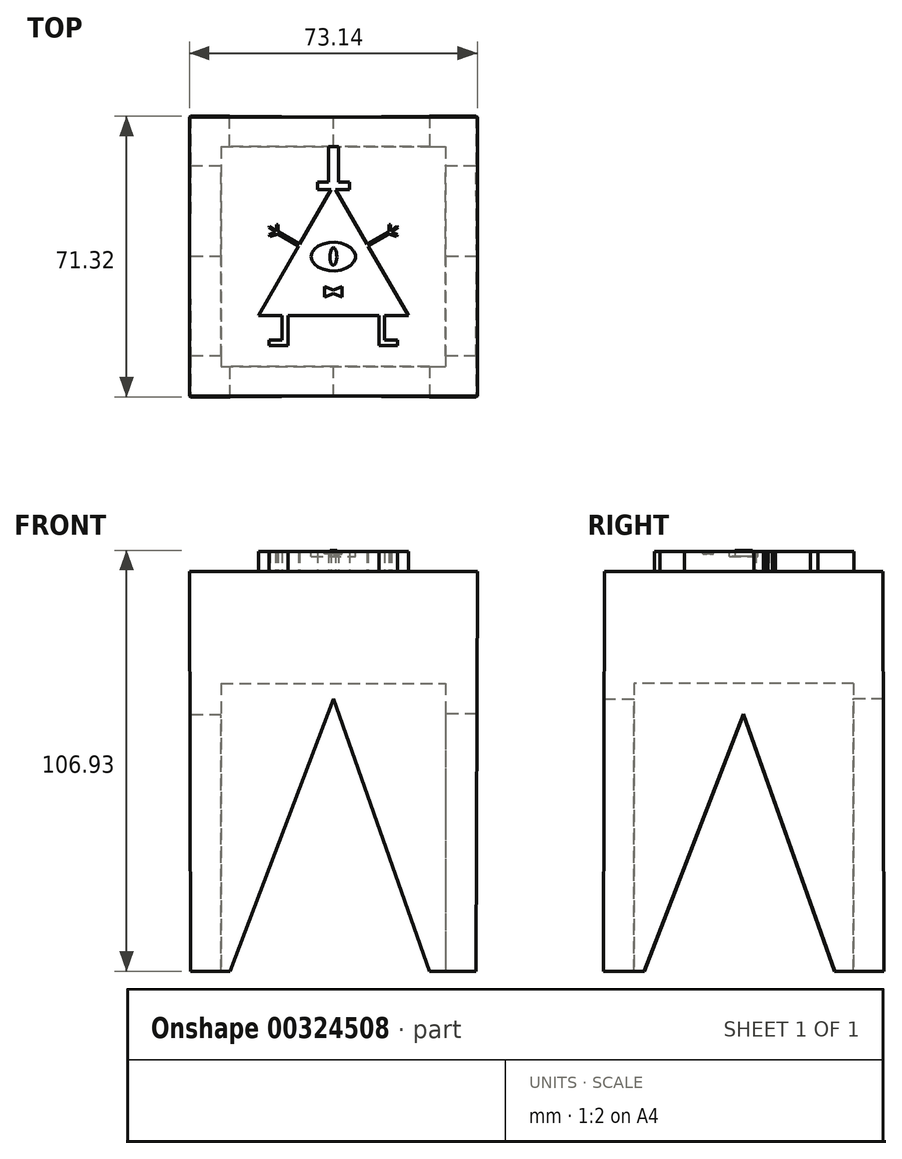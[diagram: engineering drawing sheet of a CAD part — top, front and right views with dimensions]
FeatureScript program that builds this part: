
annotation { "Feature Type Name" : "Feature", "Feature Type Description" : "" }
export const myFeature = defineFeature(function(context is Context, id is Id, definition is map)
    precondition{}
    {
        {
            var Q0;
            Q0=qCreatedBy(makeId("Top.planeOp"),FACE);
            var sketch = newSketch(context, id + "F0", { "sketchPlane" : qUnion([Q0])});
            skLineSegment(sketch, "E0.bottom", {"start": v(-36.23, 35.66) * mm, "end": v(36.23, 35.66) * mm});
            skLineSegment(sketch, "E0.top", {"start": v(-36.23, -35.66) * mm, "end": v(36.23, -35.66) * mm});
            skLineSegment(sketch, "E0.left", {"start": v(-36.23, 35.66) * mm, "end": v(-36.23, -35.66) * mm});
            skLineSegment(sketch, "E0.right", {"start": v(36.23, 35.66) * mm, "end": v(36.23, -35.66) * mm});
            skPoint(sketch, "E0.middle", {"position": v(0, 0) * mm});
            skSolve(sketch);
        }
        {
            var Q0;
            Q0=qCreatedBy(makeId("Top.planeOp"),FACE);
            cPlane(context, id + "F1", {"entities" : qUnion([Q0]), "cplaneType" : CPlaneType.OFFSET, "offset" : 101.6 * mm, "width" : 152.4 * mm, "height" : 152.4 * mm});
        }
        {
            var Q0;
            Q0=qCreatedBy(id+"F1.planeOp",FACE);
            var sketch = newSketch(context, id + "F2", { "sketchPlane" : qUnion([Q0])});
            skLineSegment(sketch, "E1.bottom", {"start": v(-36.57, 35.42) * mm, "end": v(36.57, 35.42) * mm});
            skLineSegment(sketch, "E1.top", {"start": v(-36.57, -35.42) * mm, "end": v(36.57, -35.42) * mm});
            skLineSegment(sketch, "E1.left", {"start": v(-36.57, 35.42) * mm, "end": v(-36.57, -35.42) * mm});
            skLineSegment(sketch, "E1.right", {"start": v(36.57, 35.42) * mm, "end": v(36.57, -35.42) * mm});
            skPoint(sketch, "E1.middle", {"position": v(0, 0) * mm});
            skSolve(sketch);
        }
        {
            var Q0;
            Q0=makeQuery(id+"F2.imprint","IMPRINT",FACE,{"disambiguationData":[TD([[makeQuery(id+"F2.imprint","IMPRINT",EDGE,{"derivedFrom":sQuery(id+"F2.wireOp",EDGE,"E1.bottom")}),-1.0]])]});
            var Q1;
            Q1=makeQuery(id+"F0.imprint","IMPRINT",FACE,{"disambiguationData":[TD([[makeQuery(id+"F0.imprint","IMPRINT",EDGE,{"derivedFrom":sQuery(id+"F0.wireOp",EDGE,"E0.bottom")}),-1.0]])]});
            loft(context, id + "F3", {"sheetProfilesArray" : [{ "sheetProfileEntities" : qUnion([Q0]) }, { "sheetProfileEntities" : qUnion([Q1]) }]});
        }
        {
            var Q0;
            Q0=makeQuery(id+"F3.opLoft","SWEPT_FACE",FACE,{"disambiguationData":[OSD([sQuery(id+"F0.wireOp",EDGE,"E0.bottom"),sQuery(id+"F0.wireOp",EDGE,"E0.top"),sQuery(id+"F0.wireOp",EDGE,"E0.left"),sQuery(id+"F2.wireOp",EDGE,"E1.bottom"),sQuery(id+"F2.wireOp",EDGE,"E1.top"),sQuery(id+"F2.wireOp",EDGE,"E1.left")])]});
            var sketch = newSketch(context, id + "F4", { "sketchPlane" : qUnion([Q0])});
            skLineSegment(sketch, "E2", {"start": v(-24.16, -2.93) * mm, "end": v(0, 65.28) * mm});
            skLineSegment(sketch, "E3", {"start": v(0, 65.28) * mm, "end": v(26.31, -2.66) * mm});
            skLineSegment(sketch, "E4", {"start": v(26.31, -2.66) * mm, "end": v(-24.16, -2.93) * mm});
            skSolve(sketch);
        }
        {
            var Q0;
            Q0=makeQuery(id+"F3.opLoft","CAP_FACE",FACE,{"disambiguationData":[OSD([makeQuery(id+"F0.imprint","IMPRINT",FACE,{"disambiguationData":[TD([[makeQuery(id+"F0.imprint","IMPRINT",EDGE,{"derivedFrom":sQuery(id+"F0.wireOp",EDGE,"E0.bottom")}),-1.0]])]})])],"isStart":true});
            var sketch = newSketch(context, id + "F5", { "sketchPlane" : qUnion([Q0])});
            skLineSegment(sketch, "E5.bottom", {"start": v(-28.48, -27.93) * mm, "end": v(28.48, -27.93) * mm});
            skLineSegment(sketch, "E5.top", {"start": v(-28.48, 27.93) * mm, "end": v(28.48, 27.93) * mm});
            skLineSegment(sketch, "E5.left", {"start": v(-28.48, -27.93) * mm, "end": v(-28.48, 27.93) * mm});
            skLineSegment(sketch, "E5.right", {"start": v(28.48, -27.93) * mm, "end": v(28.48, 27.93) * mm});
            skPoint(sketch, "E5.middle", {"position": v(0, 0) * mm});
            skSolve(sketch);
        }
        {
            var Q0;
            Q0 = qSketchRegion(id + "F5", true);
            extrude(context, id + "F6", {"entities" : qUnion([Q0]), "operationType" : NewBodyOperationType.REMOVE, "oppositeDirection" : true, "depth" : 73.15 * mm});
        }
        {
            var Q0;
            Q0 = qSketchRegion(id + "F4", true);
            extrude(context, id + "F7", {"entities" : qUnion([Q0]), "operationType" : NewBodyOperationType.REMOVE, "oppositeDirection" : true, "depth" : 95.76 * mm});
        }
        {
            var Q0;
            Q0=makeQuery(id+"F3.opLoft","SWEPT_FACE",FACE,{"disambiguationData":[OSD([sQuery(id+"F0.wireOp",EDGE,"E0.bottom"),sQuery(id+"F0.wireOp",EDGE,"E0.left"),sQuery(id+"F0.wireOp",EDGE,"E0.right"),sQuery(id+"F2.wireOp",EDGE,"E1.bottom"),sQuery(id+"F2.wireOp",EDGE,"E1.left"),sQuery(id+"F2.wireOp",EDGE,"E1.right")])]});
            var sketch = newSketch(context, id + "F8", { "sketchPlane" : qUnion([Q0])});
            skLineSegment(sketch, "E6", {"start": v(-25.38, -2.8) * mm, "end": v(0, 69.23) * mm});
            skLineSegment(sketch, "E7", {"start": v(0, 69.23) * mm, "end": v(27.38, -2.8) * mm});
            skLineSegment(sketch, "E8", {"start": v(27.38, -2.8) * mm, "end": v(-25.38, -2.8) * mm});
            skSolve(sketch);
        }
        {
            var Q0;
            Q0 = qSketchRegion(id + "F8", true);
            extrude(context, id + "F9", {"entities" : qUnion([Q0]), "operationType" : NewBodyOperationType.REMOVE, "oppositeDirection" : true, "depth" : 86.61 * mm});
        }
        {
            var Q0;
            Q0=makeQuery(id+"F3.opLoft","CAP_FACE",FACE,{"disambiguationData":[OSD([makeQuery(id+"F2.imprint","IMPRINT",FACE,{"disambiguationData":[TD([[makeQuery(id+"F2.imprint","IMPRINT",EDGE,{"derivedFrom":sQuery(id+"F2.wireOp",EDGE,"E1.bottom")}),-1.0]])]})])],"isStart":true});
            var sketch = newSketch(context, id + "F10", { "sketchPlane" : qUnion([Q0])});
            skLineSegment(sketch, "E9", {"start": v(-0.53, 17.03) * mm, "end": v(-8.56, 3.13) * mm});
            skLineSegment(sketch, "E10", {"start": v(-19.05, -15.04) * mm, "end": v(19.05, -15.04) * mm});
            skLineSegment(sketch, "E11", {"start": v(19.05, -15.04) * mm, "end": v(0.53, 17.03) * mm});
            skLineSegment(sketch, "E12.bottom", {"start": v(-4.06, 18.88) * mm, "end": v(-1.3, 18.88) * mm});
            skLineSegment(sketch, "E12.top", {"start": v(-4.06, 17.03) * mm, "end": v(-0.53, 17.03) * mm});
            skLineSegment(sketch, "E12.left", {"start": v(-4.06, 18.88) * mm, "end": v(-4.06, 17.03) * mm});
            skLineSegment(sketch, "E12.right", {"start": v(4.06, 18.88) * mm, "end": v(4.06, 17.03) * mm});
            skPoint(sketch, "E12.middle", {"position": v(0, 17.96) * mm});
            skLineSegment(sketch, "E13.bottom", {"start": v(-1.3, 27.99) * mm, "end": v(1.3, 27.99) * mm});
            skLineSegment(sketch, "E13.left", {"start": v(-1.3, 27.99) * mm, "end": v(-1.3, 18.62) * mm});
            skLineSegment(sketch, "E13.right", {"start": v(1.3, 27.99) * mm, "end": v(1.3, 18.62) * mm});
            skPoint(sketch, "E13.middle", {"position": v(0, 23.3) * mm});
            skLineSegment(sketch, "E14.trimOffspring", {"start": v(1.3, 18.88) * mm, "end": v(4.06, 18.88) * mm});
            skLineSegment(sketch, "E15.trimOffspring", {"start": v(0.53, 17.03) * mm, "end": v(4.06, 17.03) * mm});
            skLineSegment(sketch, "E16", {"start": v(-8.84, 2.65) * mm, "end": v(-14.11, 5.7) * mm});
            skLineSegment(sketch, "E17", {"start": v(-14.11, 6.33) * mm, "end": v(-14.11, 8.1) * mm});
            skLineSegment(sketch, "E18", {"start": v(-14.11, 8.1) * mm, "end": v(-14.46, 8.1) * mm});
            skLineSegment(sketch, "E19", {"start": v(-14.46, 8.1) * mm, "end": v(-14.46, 6.48) * mm});
            skLineSegment(sketch, "E20", {"start": v(-14.46, 6.48) * mm, "end": v(-16.2, 7.7) * mm});
            skLineSegment(sketch, "E21", {"start": v(-16.2, 7.7) * mm, "end": v(-16.38, 7.38) * mm});
            skLineSegment(sketch, "E22", {"start": v(-16.38, 7.38) * mm, "end": v(-14.74, 6.2) * mm});
            skLineSegment(sketch, "E23", {"start": v(-14.74, 6.2) * mm, "end": v(-16.28, 5.53) * mm});
            skLineSegment(sketch, "E24", {"start": v(-16.28, 5.53) * mm, "end": v(-16.08, 5.09) * mm});
            skLineSegment(sketch, "E25", {"start": v(-16.08, 5.09) * mm, "end": v(-14.11, 5.7) * mm});
            skLineSegment(sketch, "E26", {"start": v(-14.11, 6.33) * mm, "end": v(-8.56, 3.13) * mm});
            skLineSegment(sketch, "E27.trimOffspring", {"start": v(-8.84, 2.65) * mm, "end": v(-19.05, -15.04) * mm});
            skLineSegment(sketch, "E28.MirrorCS", {"start": v(14.11, 6.33) * mm, "end": v(8.56, 3.13) * mm});
            skLineSegment(sketch, "E29.MirrorCS", {"start": v(14.11, 6.33) * mm, "end": v(14.11, 8.1) * mm});
            skLineSegment(sketch, "E30.MirrorCS", {"start": v(14.11, 8.1) * mm, "end": v(14.46, 8.1) * mm});
            skLineSegment(sketch, "E31.MirrorCS", {"start": v(14.46, 8.1) * mm, "end": v(14.46, 6.48) * mm});
            skLineSegment(sketch, "E32.MirrorCS", {"start": v(14.46, 6.48) * mm, "end": v(16.2, 7.7) * mm});
            skLineSegment(sketch, "E33.MirrorCS", {"start": v(16.2, 7.7) * mm, "end": v(16.38, 7.38) * mm});
            skLineSegment(sketch, "E34.MirrorCS", {"start": v(16.38, 7.38) * mm, "end": v(14.74, 6.2) * mm});
            skLineSegment(sketch, "E35.MirrorCS", {"start": v(14.74, 6.2) * mm, "end": v(16.28, 5.53) * mm});
            skLineSegment(sketch, "E36.MirrorCS", {"start": v(16.28, 5.53) * mm, "end": v(16.08, 5.09) * mm});
            skLineSegment(sketch, "E37.MirrorCS", {"start": v(16.08, 5.09) * mm, "end": v(14.11, 5.7) * mm});
            skLineSegment(sketch, "E38.MirrorCS", {"start": v(8.84, 2.65) * mm, "end": v(14.11, 5.7) * mm});
            skPoint(sketch, "E39.end.orphan", {"position": v(0, -15.04) * mm});
            skLineSegment(sketch, "E40", {"start": v(-13.03, -15.04) * mm, "end": v(-13.03, -21.27) * mm});
            skLineSegment(sketch, "E41", {"start": v(-13.03, -21.27) * mm, "end": v(-16.32, -21.27) * mm});
            skLineSegment(sketch, "E42", {"start": v(-16.32, -21.27) * mm, "end": v(-16.32, -22.6) * mm});
            skLineSegment(sketch, "E43", {"start": v(-16.32, -22.6) * mm, "end": v(-11.55, -22.6) * mm});
            skLineSegment(sketch, "E44", {"start": v(-11.55, -22.6) * mm, "end": v(-11.55, -15.04) * mm});
            skLineSegment(sketch, "E45.MirrorCS", {"start": v(11.55, -22.6) * mm, "end": v(11.55, -15.04) * mm});
            skLineSegment(sketch, "E46.MirrorCS", {"start": v(13.03, -15.04) * mm, "end": v(13.03, -21.27) * mm});
            skLineSegment(sketch, "E47.MirrorCS", {"start": v(13.03, -21.27) * mm, "end": v(16.32, -21.27) * mm});
            skLineSegment(sketch, "E48.MirrorCS", {"start": v(16.32, -21.27) * mm, "end": v(16.32, -22.6) * mm});
            skLineSegment(sketch, "E49.MirrorCS", {"start": v(16.32, -22.6) * mm, "end": v(11.55, -22.6) * mm});
            skSolve(sketch);
        }
        {
            var Q0;
            Q0 = qSketchRegion(id + "F10", true);
            extrude(context, id + "F11", {"entities" : qUnion([Q0]), "operationType" : NewBodyOperationType.ADD, "depth" : 5.08 * mm});
        }
        {
            var Q0;
            Q0=makeQuery(id+"F11.opExtrude","CAP_FACE",FACE,{"disambiguationData":[OSD([sQuery(id+"F10.wireOp",EDGE,"E9"),sQuery(id+"F10.wireOp",EDGE,"E10"),sQuery(id+"F10.wireOp",EDGE,"E11")])],"isStart":false});
            var sketch = newSketch(context, id + "F12", { "sketchPlane" : qUnion([Q0])});
            skEllipse(sketch, "E50", {"center": v(0, 0) * mm, "majorRadius": 3.64 * mm, "minorRadius": 5.62 * mm, "majorAxis": v(0, 1)});
            skSolve(sketch);
        }
        {
            var Q0;
            Q0 = qSketchRegion(id + "F12", true);
            extrude(context, id + "F13", {"entities" : qUnion([Q0]), "operationType" : NewBodyOperationType.REMOVE, "oppositeDirection" : true, "depth" : 1.27 * mm});
        }
        {
            var Q0;
            Q0=makeQuery(id+"F13.boolean.opBoolean","COPY",FACE,{"derivedFrom":makeQuery(id+"F13.opExtrude","CAP_FACE",FACE,{"disambiguationData":[OSD([sQuery(id+"F12.wireOp",EDGE,"E50")])],"isStart":false})});
            var sketch = newSketch(context, id + "F14", { "sketchPlane" : qUnion([Q0])});
            skEllipse(sketch, "E51", {"center": v(0, 0) * mm, "majorRadius": 2.24 * mm, "minorRadius": 0.87 * mm, "majorAxis": v(0, 1)});
            skSolve(sketch);
        }
        {
            var Q0;
            Q0 = qSketchRegion(id + "F14", true);
            extrude(context, id + "F15", {"entities" : qUnion([Q0]), "operationType" : NewBodyOperationType.ADD, "depth" : 1.52 * mm});
        }
        {
            var Q0;
            Q0=makeQuery(id+"F11.opExtrude","CAP_FACE",FACE,{"disambiguationData":[OSD([sQuery(id+"F10.wireOp",EDGE,"E9"),sQuery(id+"F10.wireOp",EDGE,"E10"),sQuery(id+"F10.wireOp",EDGE,"E11"),sQuery(id+"F10.wireOp",EDGE,"E12.bottom"),sQuery(id+"F10.wireOp",EDGE,"E12.top"),sQuery(id+"F10.wireOp",EDGE,"E12.left"),sQuery(id+"F10.wireOp",EDGE,"E12.right"),sQuery(id+"F10.wireOp",EDGE,"E13.bottom"),sQuery(id+"F10.wireOp",EDGE,"E13.left"),sQuery(id+"F10.wireOp",EDGE,"E13.right"),sQuery(id+"F10.wireOp",EDGE,"E14.trimOffspring"),sQuery(id+"F10.wireOp",EDGE,"E15.trimOffspring"),sQuery(id+"F10.wireOp",EDGE,"E16"),sQuery(id+"F10.wireOp",EDGE,"E17"),sQuery(id+"F10.wireOp",EDGE,"E18"),sQuery(id+"F10.wireOp",EDGE,"E19"),sQuery(id+"F10.wireOp",EDGE,"E20"),sQuery(id+"F10.wireOp",EDGE,"E21"),sQuery(id+"F10.wireOp",EDGE,"E22"),sQuery(id+"F10.wireOp",EDGE,"E23"),sQuery(id+"F10.wireOp",EDGE,"E24"),sQuery(id+"F10.wireOp",EDGE,"E25"),sQuery(id+"F10.wireOp",EDGE,"E26"),sQuery(id+"F10.wireOp",EDGE,"E27.trimOffspring"),sQuery(id+"F10.wireOp",EDGE,"E28.MirrorCS"),sQuery(id+"F10.wireOp",EDGE,"E29.MirrorCS"),sQuery(id+"F10.wireOp",EDGE,"E30.MirrorCS"),sQuery(id+"F10.wireOp",EDGE,"E31.MirrorCS"),sQuery(id+"F10.wireOp",EDGE,"E32.MirrorCS"),sQuery(id+"F10.wireOp",EDGE,"E33.MirrorCS"),sQuery(id+"F10.wireOp",EDGE,"E34.MirrorCS"),sQuery(id+"F10.wireOp",EDGE,"E35.MirrorCS"),sQuery(id+"F10.wireOp",EDGE,"E36.MirrorCS"),sQuery(id+"F10.wireOp",EDGE,"E37.MirrorCS"),sQuery(id+"F10.wireOp",EDGE,"E38.MirrorCS"),sQuery(id+"F10.wireOp",EDGE,"E40"),sQuery(id+"F10.wireOp",EDGE,"E41"),sQuery(id+"F10.wireOp",EDGE,"E42"),sQuery(id+"F10.wireOp",EDGE,"E43"),sQuery(id+"F10.wireOp",EDGE,"E44"),sQuery(id+"F10.wireOp",EDGE,"E45.MirrorCS"),sQuery(id+"F10.wireOp",EDGE,"E46.MirrorCS"),sQuery(id+"F10.wireOp",EDGE,"E47.MirrorCS"),sQuery(id+"F10.wireOp",EDGE,"E48.MirrorCS"),sQuery(id+"F10.wireOp",EDGE,"E49.MirrorCS")])],"isStart":false});
            var sketch = newSketch(context, id + "F16", { "sketchPlane" : qUnion([Q0])});
            skPoint(sketch, "E52.orphan", {"position": v(0, 0) * mm});
            skPoint(sketch, "E53.end.orphan", {"position": v(0, -15.04) * mm});
            skLineSegment(sketch, "E54", {"start": v(0, -8.53) * mm, "end": v(-2.22, -7.62) * mm});
            skLineSegment(sketch, "E55", {"start": v(-2.22, -7.62) * mm, "end": v(-2.22, -10.29) * mm});
            skLineSegment(sketch, "E56", {"start": v(-2.22, -10.29) * mm, "end": v(0, -9.34) * mm});
            skLineSegment(sketch, "E57.MirrorCS", {"start": v(0, -8.53) * mm, "end": v(2.22, -7.62) * mm});
            skLineSegment(sketch, "E58.MirrorCS", {"start": v(2.22, -7.62) * mm, "end": v(2.22, -10.29) * mm});
            skLineSegment(sketch, "E59.MirrorCS", {"start": v(2.22, -10.29) * mm, "end": v(0, -9.34) * mm});
            skSolve(sketch);
        }
        {
            var Q0;
            Q0 = qSketchRegion(id + "F16", true);
            extrude(context, id + "F17", {"entities" : qUnion([Q0]), "operationType" : NewBodyOperationType.REMOVE, "oppositeDirection" : true, "depth" : 0.71 * mm});
        }
    });
